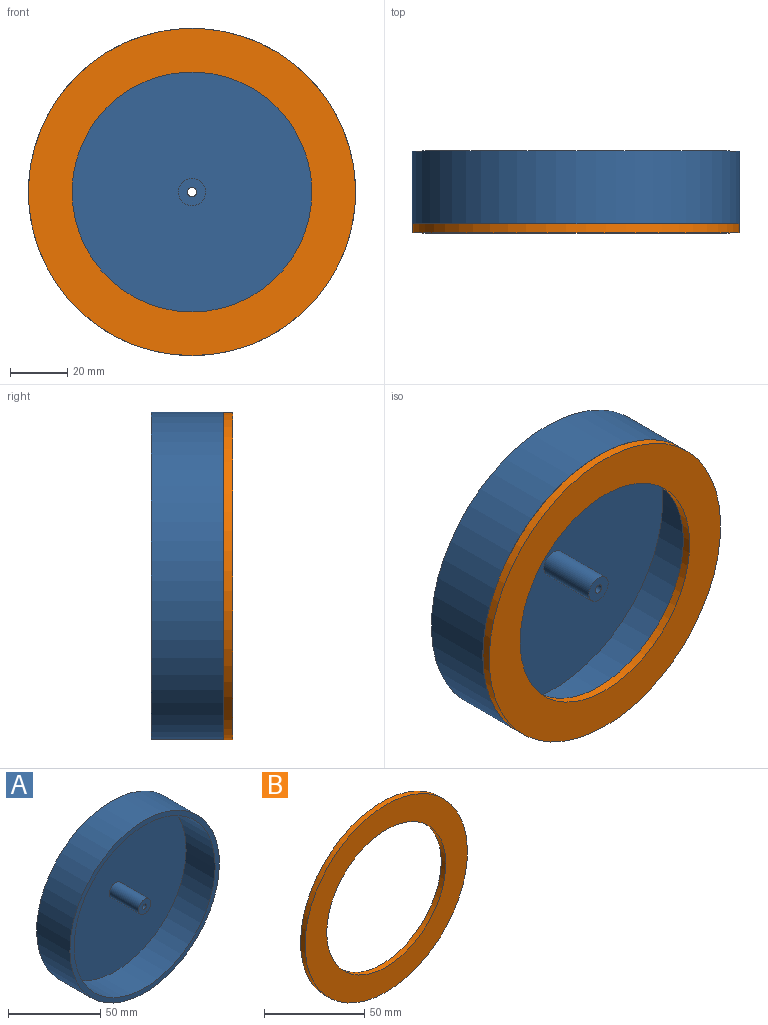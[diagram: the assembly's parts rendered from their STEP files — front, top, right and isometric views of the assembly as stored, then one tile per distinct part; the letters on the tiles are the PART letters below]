
ASSEMBLY  parts=2 mates=1
PART A: 8 faces, bbox 114.3x25.4x114.3 mm
  f0: cylinder r=53.98mm len=107.95mm, axis (0,1,0), area 7537.3mm2, adj f1,f4
  f1: plane 107.95x107.95mm, normal (0,-1,0), area 9081.1mm2, adj f0,f5
  f2: plane 114.3x114.3mm, normal (0,1,0), area 10252.9mm2, adj f3,f7
  f3: cylinder r=57.15mm len=114.3mm, axis (0,1,0), area 9120.7mm2, adj f2,f4
  f4: plane 114.3x114.3mm, normal (0,-1,0), area 1108.4mm2, adj f0,f3
  f5: cylinder r=4.76mm len=22.23mm, axis (0,1,0), area 665.1mm2, adj f1,f6
  f6: plane 9.53x9.53mm, normal (0,-1,0), area 63.3mm2, adj f5,f7
  f7: cylinder r=1.59mm len=25.4mm, axis (0,-1,0), area 253.4mm2, adj f2,f6
PART B: 4 faces, bbox 114.3x3.2x114.3 mm
  f0: cylinder r=41.89mm len=83.78mm, axis (0,1,0), area 835.7mm2, adj f2,f3
  f1: cylinder r=57.15mm len=114.3mm, axis (0,1,0), area 1140.1mm2, adj f2,f3
  f2: plane 114.3x114.3mm, normal (0,-1,0), area 4747.4mm2, adj f0,f1
  f3: plane 114.3x114.3mm, normal (0,1,0), area 4747.4mm2, adj f0,f1
PLACE A at identity
PLACE B t=(0,-25.4,0)mm
MATE fastened B.f1 <-> A.f0  axis (0,1,0) through (0,-25.4,0)mm
